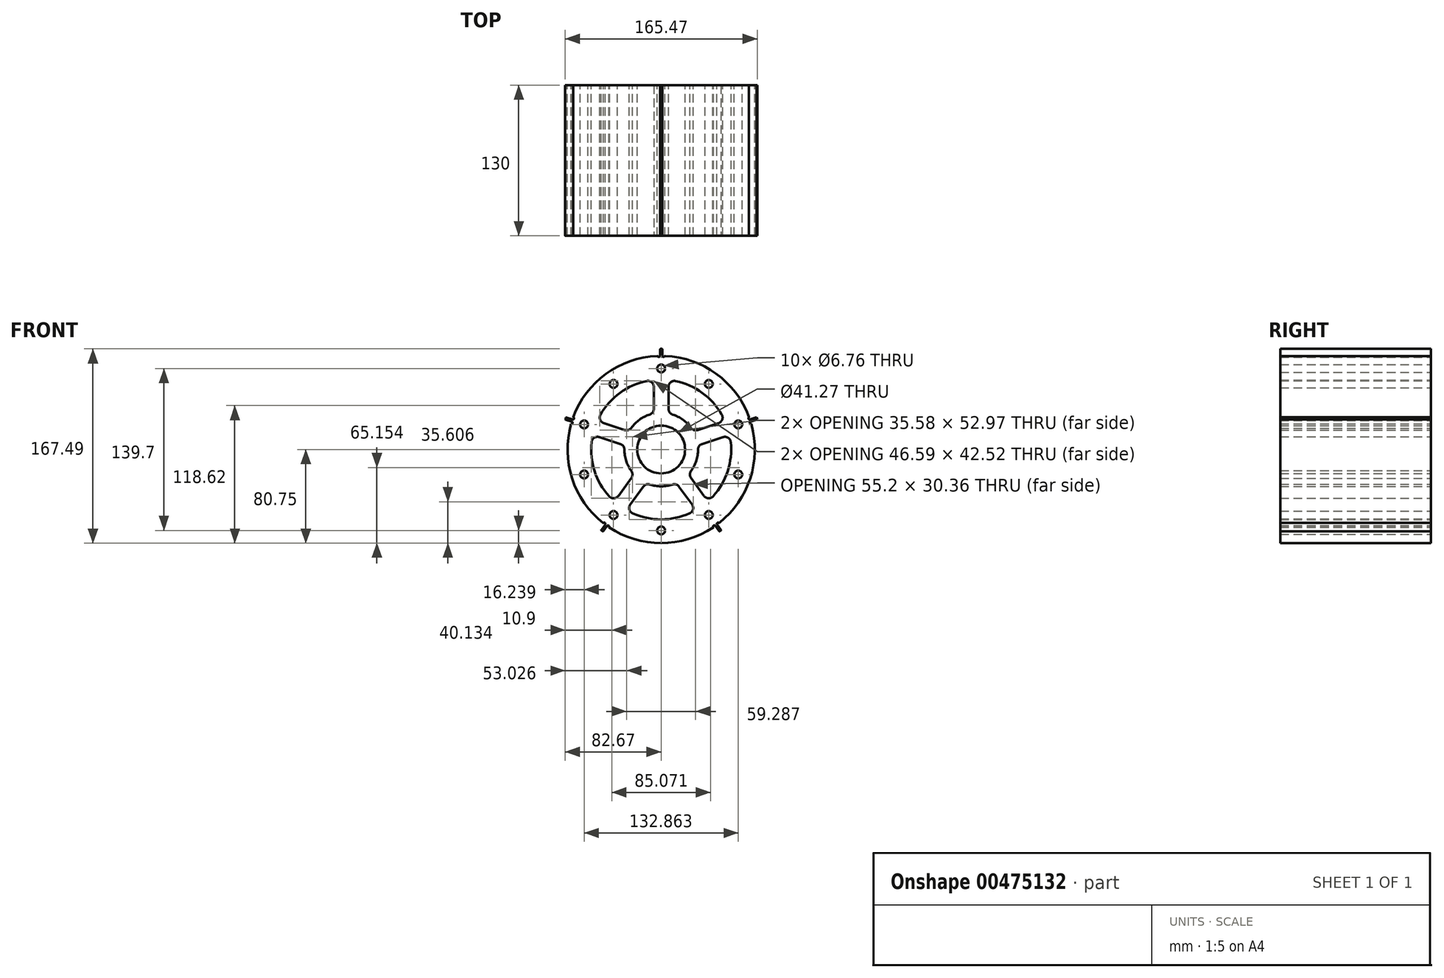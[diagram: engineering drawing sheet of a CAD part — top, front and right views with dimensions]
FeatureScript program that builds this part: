
annotation { "Feature Type Name" : "Feature", "Feature Type Description" : "" }
export const myFeature = defineFeature(function(context is Context, id is Id, definition is map)
    precondition{}
    {
        {
            var Q0;
            Q0=qCreatedBy(makeId("Front.planeOp"),FACE);
            var sketch = newSketch(context, id + "F0", { "sketchPlane" : qUnion([Q0])});
            skArc(sketch, "E0", {"start": v(-1, 80.74) * mm, "mid": v(-47.46, 65.33) * mm, "end": v(-76.48, 25.9) * mm});
            skLineSegment(sketch, "E1", {"start": v(0, 0) * mm, "end": v(0, 93.04) * mm, "construction": true});
            skLineSegment(sketch, "E2", {"start": v(-1, 86.74) * mm, "end": v(-1, 80.74) * mm});
            skLineSegment(sketch, "E3.MirrorCS", {"start": v(1, 86.74) * mm, "end": v(1, 80.74) * mm});
            skLineSegment(sketch, "E4", {"start": v(-1, 86.74) * mm, "end": v(1, 86.74) * mm});
            skLineSegment(sketch, "E5.1.0", {"start": v(-82.18, 27.75) * mm, "end": v(-76.48, 25.9) * mm});
            skLineSegment(sketch, "E5.1.1", {"start": v(-82.8, 25.85) * mm, "end": v(-82.18, 27.75) * mm});
            skLineSegment(sketch, "E5.1.2", {"start": v(-82.8, 25.85) * mm, "end": v(-77.1, 24) * mm});
            skLineSegment(sketch, "E5.2.0", {"start": v(-51.8, -69.58) * mm, "end": v(-48.27, -64.73) * mm});
            skLineSegment(sketch, "E5.2.1", {"start": v(-50.17, -70.76) * mm, "end": v(-51.8, -69.58) * mm});
            skLineSegment(sketch, "E5.2.2", {"start": v(-50.17, -70.76) * mm, "end": v(-46.65, -65.91) * mm});
            skLineSegment(sketch, "E5.3.0", {"start": v(50.17, -70.76) * mm, "end": v(46.65, -65.91) * mm});
            skLineSegment(sketch, "E5.3.1", {"start": v(51.8, -69.58) * mm, "end": v(50.17, -70.76) * mm});
            skLineSegment(sketch, "E5.3.2", {"start": v(51.8, -69.58) * mm, "end": v(48.27, -64.73) * mm});
            skArc(sketch, "E6.trimOffspring", {"start": v(-77.1, 24) * mm, "mid": v(-76.8, -24.95) * mm, "end": v(-48.27, -64.73) * mm});
            skArc(sketch, "E7.trimOffspring", {"start": v(76.48, 25.9) * mm, "mid": v(47.46, 65.33) * mm, "end": v(1, 80.74) * mm});
            skArc(sketch, "E8.trimOffspring", {"start": v(-46.65, -65.91) * mm, "mid": v(47.46, -65.33) * mm, "end": v(77.1, 24) * mm});
            skLineSegment(sketch, "E9.2.4.0", {"start": v(82.8, 25.85) * mm, "end": v(77.1, 24) * mm});
            skLineSegment(sketch, "E9.3.4.0", {"start": v(82.18, 27.75) * mm, "end": v(82.8, 25.85) * mm});
            skLineSegment(sketch, "E9.6.4.0", {"start": v(82.18, 27.75) * mm, "end": v(76.48, 25.9) * mm});
            skSolve(sketch);
        }
        {
            var Q0;
            Q0 = qSketchRegion(id + "F0", true);
            extrude(context, id + "F1", {"entities" : qUnion([Q0]), "depth" : 130 * mm});
        }
        {
            var Q0;
            Q0=qCreatedBy(makeId("Front.planeOp"),FACE);
            var sketch = newSketch(context, id + "F2", { "sketchPlane" : qUnion([Q0])});
            skCircle(sketch, "E10", {"center": v(0, 0) * mm, "radius": 20.64 * mm});
            skSolve(sketch);
        }
        {
            var Q0;
            Q0=makeQuery(id+"F2.imprint","IMPRINT",FACE,{"disambiguationData":[TD([[makeQuery(id+"F2.imprint","IMPRINT",EDGE,{"derivedFrom":sQuery(id+"F2.wireOp",EDGE,"E10")}),1.0]])]});
            var Q1;
            Q1=makeQuery(id+"F1.opExtrude","CAP_FACE",FACE,{"disambiguationData":[OSD([sQuery(id+"F0.wireOp",EDGE,"E0"),sQuery(id+"F0.wireOp",EDGE,"E2"),sQuery(id+"F0.wireOp",EDGE,"E3.MirrorCS"),sQuery(id+"F0.wireOp",EDGE,"E4"),sQuery(id+"F0.wireOp",EDGE,"E5.1.0"),sQuery(id+"F0.wireOp",EDGE,"E5.1.1"),sQuery(id+"F0.wireOp",EDGE,"E5.1.2"),sQuery(id+"F0.wireOp",EDGE,"E5.2.0"),sQuery(id+"F0.wireOp",EDGE,"E5.2.1"),sQuery(id+"F0.wireOp",EDGE,"E5.2.2"),sQuery(id+"F0.wireOp",EDGE,"E5.3.0"),sQuery(id+"F0.wireOp",EDGE,"E5.3.1"),sQuery(id+"F0.wireOp",EDGE,"E5.3.2"),sQuery(id+"F0.wireOp",EDGE,"E6.trimOffspring"),sQuery(id+"F0.wireOp",EDGE,"E7.trimOffspring"),sQuery(id+"F0.wireOp",EDGE,"E8.trimOffspring")])],"isStart":false});
            extrude(context, id + "F3", {"entities" : qUnion([Q0]), "operationType" : NewBodyOperationType.REMOVE, "endBound" : BoundingType.UP_TO_SURFACE, "endBoundEntityFace" : qUnion([Q1]), "depth" : 25.4 * mm});
        }
        {
            var Q0;
            Q0=qCreatedBy(makeId("Front.planeOp"),FACE);
            var sketch = newSketch(context, id + "F4", { "sketchPlane" : qUnion([Q0])});
            skLineSegment(sketch, "E11", {"start": v(9.9, 57.53) * mm, "end": v(9.9, 35.38) * mm});
            skLineSegment(sketch, "E12", {"start": v(35.38, 9.9) * mm, "end": v(57.53, 9.9) * mm});
            skArc(sketch, "E13", {"start": v(66.9, 23.04) * mm, "mid": v(50.03, 50.03) * mm, "end": v(23.04, 66.9) * mm});
            skArc(sketch, "E14", {"start": v(26.73, 14.97) * mm, "mid": v(21.67, 21.67) * mm, "end": v(14.97, 26.73) * mm});
            skArc(sketch, "E15.filletArc", {"start": v(26.73, 14.97) * mm, "mid": v(30.37, 11.27) * mm, "end": v(35.38, 9.9) * mm});
            skArc(sketch, "E16.filletArc", {"start": v(9.9, 35.38) * mm, "mid": v(11.27, 30.37) * mm, "end": v(14.97, 26.73) * mm});
            skArc(sketch, "E17.filletArc", {"start": v(23.04, 66.9) * mm, "mid": v(14.06, 65.6) * mm, "end": v(9.9, 57.53) * mm});
            skArc(sketch, "E18.filletArc", {"start": v(57.53, 9.9) * mm, "mid": v(65.6, 14.06) * mm, "end": v(66.9, 23.04) * mm});
            skLineSegment(sketch, "E19", {"start": v(0, 0) * mm, "end": v(0, 68.56) * mm, "construction": true});
            skLineSegment(sketch, "E20", {"start": v(0, 0) * mm, "end": v(60.99, 0) * mm, "construction": true});
            skLineSegment(sketch, "E21.1.0", {"start": v(-57.53, 9.9) * mm, "end": v(-35.38, 9.9) * mm});
            skArc(sketch, "E21.1.1", {"start": v(-66.9, 23.04) * mm, "mid": v(-65.6, 14.06) * mm, "end": v(-57.53, 9.9) * mm});
            skArc(sketch, "E21.1.2", {"start": v(-23.04, 66.9) * mm, "mid": v(-50.03, 50.03) * mm, "end": v(-66.9, 23.04) * mm});
            skArc(sketch, "E21.1.3", {"start": v(-9.9, 57.53) * mm, "mid": v(-14.06, 65.6) * mm, "end": v(-23.04, 66.9) * mm});
            skLineSegment(sketch, "E21.1.4", {"start": v(-9.9, 35.38) * mm, "end": v(-9.9, 57.53) * mm});
            skArc(sketch, "E21.1.5", {"start": v(-14.97, 26.73) * mm, "mid": v(-11.27, 30.37) * mm, "end": v(-9.9, 35.38) * mm});
            skArc(sketch, "E21.1.6", {"start": v(-35.38, 9.9) * mm, "mid": v(-30.37, 11.27) * mm, "end": v(-26.73, 14.97) * mm});
            skArc(sketch, "E21.1.7", {"start": v(-14.97, 26.73) * mm, "mid": v(-21.67, 21.67) * mm, "end": v(-26.73, 14.97) * mm});
            skLineSegment(sketch, "E21.2.0", {"start": v(-9.9, -57.53) * mm, "end": v(-9.9, -35.38) * mm});
            skArc(sketch, "E21.2.1", {"start": v(-23.04, -66.9) * mm, "mid": v(-14.06, -65.6) * mm, "end": v(-9.9, -57.53) * mm});
            skArc(sketch, "E21.2.2", {"start": v(-66.9, -23.04) * mm, "mid": v(-50.03, -50.03) * mm, "end": v(-23.04, -66.9) * mm});
            skArc(sketch, "E21.2.3", {"start": v(-57.53, -9.9) * mm, "mid": v(-65.6, -14.06) * mm, "end": v(-66.9, -23.04) * mm});
            skLineSegment(sketch, "E21.2.4", {"start": v(-35.38, -9.9) * mm, "end": v(-57.53, -9.9) * mm});
            skArc(sketch, "E21.2.5", {"start": v(-26.73, -14.97) * mm, "mid": v(-30.37, -11.27) * mm, "end": v(-35.38, -9.9) * mm});
            skArc(sketch, "E21.2.6", {"start": v(-9.9, -35.38) * mm, "mid": v(-11.27, -30.37) * mm, "end": v(-14.97, -26.73) * mm});
            skArc(sketch, "E21.2.7", {"start": v(-26.73, -14.97) * mm, "mid": v(-21.67, -21.67) * mm, "end": v(-14.97, -26.73) * mm});
            skLineSegment(sketch, "E21.3.0", {"start": v(57.53, -9.9) * mm, "end": v(35.38, -9.9) * mm});
            skArc(sketch, "E21.3.1", {"start": v(66.9, -23.04) * mm, "mid": v(65.6, -14.06) * mm, "end": v(57.53, -9.9) * mm});
            skArc(sketch, "E21.3.2", {"start": v(23.04, -66.9) * mm, "mid": v(50.03, -50.03) * mm, "end": v(66.9, -23.04) * mm});
            skArc(sketch, "E21.3.3", {"start": v(9.9, -57.53) * mm, "mid": v(14.06, -65.6) * mm, "end": v(23.04, -66.9) * mm});
            skLineSegment(sketch, "E21.3.4", {"start": v(9.9, -35.38) * mm, "end": v(9.9, -57.53) * mm});
            skArc(sketch, "E21.3.5", {"start": v(14.97, -26.73) * mm, "mid": v(11.27, -30.37) * mm, "end": v(9.9, -35.38) * mm});
            skArc(sketch, "E21.3.6", {"start": v(35.38, -9.9) * mm, "mid": v(30.37, -11.27) * mm, "end": v(26.73, -14.97) * mm});
            skArc(sketch, "E21.3.7", {"start": v(14.97, -26.73) * mm, "mid": v(21.67, -21.67) * mm, "end": v(26.73, -14.97) * mm});
            skSolve(sketch);
        }
        {
            var Q0;
            Q0=makeQuery(id+"F1.opExtrude","CAP_FACE",FACE,{"disambiguationData":[OSD([sQuery(id+"F0.wireOp",EDGE,"E0"),sQuery(id+"F0.wireOp",EDGE,"E2"),sQuery(id+"F0.wireOp",EDGE,"E3.MirrorCS"),sQuery(id+"F0.wireOp",EDGE,"E4"),sQuery(id+"F0.wireOp",EDGE,"E5.1.0"),sQuery(id+"F0.wireOp",EDGE,"E5.1.1"),sQuery(id+"F0.wireOp",EDGE,"E5.1.2"),sQuery(id+"F0.wireOp",EDGE,"E5.2.0"),sQuery(id+"F0.wireOp",EDGE,"E5.2.1"),sQuery(id+"F0.wireOp",EDGE,"E5.2.2"),sQuery(id+"F0.wireOp",EDGE,"E5.3.0"),sQuery(id+"F0.wireOp",EDGE,"E5.3.1"),sQuery(id+"F0.wireOp",EDGE,"E5.3.2"),sQuery(id+"F0.wireOp",EDGE,"E6.trimOffspring"),sQuery(id+"F0.wireOp",EDGE,"E7.trimOffspring"),sQuery(id+"F0.wireOp",EDGE,"E8.trimOffspring")])],"isStart":true});
            var sketch = newSketch(context, id + "F5", { "sketchPlane" : qUnion([Q0])});
            skLineSegment(sketch, "E22", {"start": v(-1, 80.74) * mm, "end": v(-7.67, 80.74) * mm, "construction": true});
            skCircle(sketch, "E23", {"center": v(-2.02, 80.74) * mm, "radius": 1.02 * mm});
            skCircle(sketch, "E24.MirrorC", {"center": v(2.02, 80.74) * mm, "radius": 1.02 * mm});
            skCircle(sketch, "E25.1.0", {"center": v(-76.17, 26.87) * mm, "radius": 1.02 * mm});
            skCircle(sketch, "E25.1.1", {"center": v(-77.41, 23.03) * mm, "radius": 1.02 * mm});
            skCircle(sketch, "E25.2.0", {"center": v(-49.1, -64.14) * mm, "radius": 1.02 * mm});
            skCircle(sketch, "E25.2.1", {"center": v(-45.83, -66.5) * mm, "radius": 1.02 * mm});
            skCircle(sketch, "E25.3.0", {"center": v(45.83, -66.5) * mm, "radius": 1.02 * mm});
            skCircle(sketch, "E25.3.1", {"center": v(49.1, -64.14) * mm, "radius": 1.02 * mm});
            skPoint(sketch, "E25.center", {"position": v(0, 0) * mm});
            skCircle(sketch, "E26.1.4.0", {"center": v(77.41, 23.03) * mm, "radius": 1.02 * mm});
            skCircle(sketch, "E26.2.4.0", {"center": v(76.17, 26.87) * mm, "radius": 1.02 * mm});
            skSolve(sketch);
        }
        {
            var Q0;
            Q0 = qSketchRegion(id + "F5", true);
            extrude(context, id + "F6", {"entities" : qUnion([Q0]), "operationType" : NewBodyOperationType.REMOVE, "endBound" : BoundingType.THROUGH_ALL, "oppositeDirection" : true, "depth" : 25.4 * mm});
        }
        {
            var Q0;
            Q0=makeQuery(id+"F1.opExtrude","SWEPT_EDGE",EDGE,{"disambiguationData":[OSD([sQuery(id+"F0.wireOp",EDGE,"E2"),sQuery(id+"F0.wireOp",EDGE,"E4")])]});
            var Q1;
            Q1=makeQuery(id+"F1.opExtrude","SWEPT_EDGE",EDGE,{"disambiguationData":[OSD([sQuery(id+"F0.wireOp",EDGE,"E3.MirrorCS"),sQuery(id+"F0.wireOp",EDGE,"E4")])]});
            var Q2;
            Q2=makeQuery(id+"F6.boolean.opBoolean","INTERSECT",EDGE,{"derivedFrom":[makeQuery(id+"F1.opExtrude","SWEPT_FACE",FACE,{"disambiguationData":[OSD([sQuery(id+"F0.wireOp",EDGE,"E0")])]}),makeQuery(id+"F6.opExtrude","SWEPT_FACE",FACE,{"disambiguationData":[OSD([sQuery(id+"F5.wireOp",EDGE,"E24.MirrorC")])]})]});
            var Q3;
            Q3=makeQuery(id+"F6.boolean.opBoolean","INTERSECT",EDGE,{"derivedFrom":[makeQuery(id+"F1.opExtrude","SWEPT_FACE",FACE,{"disambiguationData":[OSD([sQuery(id+"F0.wireOp",EDGE,"E7.trimOffspring")])]}),makeQuery(id+"F6.opExtrude","SWEPT_FACE",FACE,{"disambiguationData":[OSD([sQuery(id+"F5.wireOp",EDGE,"E23")])]})]});
            var Q4;
            Q4=makeQuery(id+"F6.boolean.opBoolean","INTERSECT",EDGE,{"derivedFrom":[makeQuery(id+"F1.opExtrude","SWEPT_FACE",FACE,{"disambiguationData":[OSD([sQuery(id+"F0.wireOp",EDGE,"E0")])]}),makeQuery(id+"F6.opExtrude","SWEPT_FACE",FACE,{"disambiguationData":[OSD([sQuery(id+"F5.wireOp",EDGE,"E25.3.1")])]})]});
            var Q5;
            Q5=makeQuery(id+"F1.opExtrude","SWEPT_EDGE",EDGE,{"disambiguationData":[OSD([sQuery(id+"F0.wireOp",EDGE,"E5.1.0"),sQuery(id+"F0.wireOp",EDGE,"E5.1.1")])]});
            var Q6;
            Q6=makeQuery(id+"F1.opExtrude","SWEPT_EDGE",EDGE,{"disambiguationData":[OSD([sQuery(id+"F0.wireOp",EDGE,"E5.1.1"),sQuery(id+"F0.wireOp",EDGE,"E5.1.2")])]});
            var Q7;
            Q7=makeQuery(id+"F6.boolean.opBoolean","INTERSECT",EDGE,{"derivedFrom":[makeQuery(id+"F1.opExtrude","SWEPT_FACE",FACE,{"disambiguationData":[OSD([sQuery(id+"F0.wireOp",EDGE,"E6.trimOffspring")])]}),makeQuery(id+"F6.opExtrude","SWEPT_FACE",FACE,{"disambiguationData":[OSD([sQuery(id+"F5.wireOp",EDGE,"E25.3.0")])]})]});
            var Q8;
            Q8=makeQuery(id+"F6.boolean.opBoolean","INTERSECT",EDGE,{"derivedFrom":[makeQuery(id+"F1.opExtrude","SWEPT_FACE",FACE,{"disambiguationData":[OSD([sQuery(id+"F0.wireOp",EDGE,"E6.trimOffspring")])]}),makeQuery(id+"F6.opExtrude","SWEPT_FACE",FACE,{"disambiguationData":[OSD([sQuery(id+"F5.wireOp",EDGE,"E25.2.1")])]})]});
            var Q9;
            Q9=makeQuery(id+"F1.opExtrude","SWEPT_EDGE",EDGE,{"disambiguationData":[OSD([sQuery(id+"F0.wireOp",EDGE,"E5.2.0"),sQuery(id+"F0.wireOp",EDGE,"E5.2.1")])]});
            var Q10;
            Q10=makeQuery(id+"F1.opExtrude","SWEPT_EDGE",EDGE,{"disambiguationData":[OSD([sQuery(id+"F0.wireOp",EDGE,"E5.2.1"),sQuery(id+"F0.wireOp",EDGE,"E5.2.2")])]});
            var Q11;
            Q11=makeQuery(id+"F6.boolean.opBoolean","INTERSECT",EDGE,{"derivedFrom":[makeQuery(id+"F1.opExtrude","SWEPT_FACE",FACE,{"disambiguationData":[OSD([sQuery(id+"F0.wireOp",EDGE,"E8.trimOffspring")])]}),makeQuery(id+"F6.opExtrude","SWEPT_FACE",FACE,{"disambiguationData":[OSD([sQuery(id+"F5.wireOp",EDGE,"E25.2.0")])]})]});
            var Q12;
            Q12=makeQuery(id+"F6.boolean.opBoolean","INTERSECT",EDGE,{"derivedFrom":[makeQuery(id+"F1.opExtrude","SWEPT_FACE",FACE,{"disambiguationData":[OSD([sQuery(id+"F0.wireOp",EDGE,"E8.trimOffspring")])]}),makeQuery(id+"F6.opExtrude","SWEPT_FACE",FACE,{"disambiguationData":[OSD([sQuery(id+"F5.wireOp",EDGE,"E25.1.1")])]})]});
            var Q13;
            Q13=makeQuery(id+"F1.opExtrude","SWEPT_EDGE",EDGE,{"disambiguationData":[OSD([sQuery(id+"F0.wireOp",EDGE,"E5.3.0"),sQuery(id+"F0.wireOp",EDGE,"E5.3.1")])]});
            var Q14;
            Q14=makeQuery(id+"F1.opExtrude","SWEPT_EDGE",EDGE,{"disambiguationData":[OSD([sQuery(id+"F0.wireOp",EDGE,"E5.3.1"),sQuery(id+"F0.wireOp",EDGE,"E5.3.2")])]});
            var Q15;
            Q15=makeQuery(id+"F6.boolean.opBoolean","INTERSECT",EDGE,{"derivedFrom":[makeQuery(id+"F1.opExtrude","SWEPT_FACE",FACE,{"disambiguationData":[OSD([sQuery(id+"F0.wireOp",EDGE,"E7.trimOffspring")])]}),makeQuery(id+"F6.opExtrude","SWEPT_FACE",FACE,{"disambiguationData":[OSD([sQuery(id+"F5.wireOp",EDGE,"E25.1.0")])]})]});
            fillet(context, id + "F7", {"entities" : qUnion([Q0, Q1, Q2, Q3, Q4, Q5, Q6, Q7, Q8, Q9, Q10, Q11, Q12, Q13, Q14, Q15]), "radius" : 0.5 * mm, "tangentPropagation" : true, "allowEdgeOverflow" : false});
        }
        {
            var Q0;
            Q0=makeQuery(id+"F1.opExtrude","CAP_FACE",FACE,{"disambiguationData":[OSD([sQuery(id+"F0.wireOp",EDGE,"E0"),sQuery(id+"F0.wireOp",EDGE,"E2"),sQuery(id+"F0.wireOp",EDGE,"E3.MirrorCS"),sQuery(id+"F0.wireOp",EDGE,"E4"),sQuery(id+"F0.wireOp",EDGE,"E5.1.0"),sQuery(id+"F0.wireOp",EDGE,"E5.1.1"),sQuery(id+"F0.wireOp",EDGE,"E5.1.2"),sQuery(id+"F0.wireOp",EDGE,"E5.2.0"),sQuery(id+"F0.wireOp",EDGE,"E5.2.1"),sQuery(id+"F0.wireOp",EDGE,"E5.2.2"),sQuery(id+"F0.wireOp",EDGE,"E5.3.0"),sQuery(id+"F0.wireOp",EDGE,"E5.3.1"),sQuery(id+"F0.wireOp",EDGE,"E5.3.2"),sQuery(id+"F0.wireOp",EDGE,"E6.trimOffspring"),sQuery(id+"F0.wireOp",EDGE,"E7.trimOffspring"),sQuery(id+"F0.wireOp",EDGE,"E8.trimOffspring"),sQuery(id+"F0.wireOp",EDGE,"E9.2.4.0"),sQuery(id+"F0.wireOp",EDGE,"E9.3.4.0"),sQuery(id+"F0.wireOp",EDGE,"E9.6.4.0")])],"isStart":true});
            var sketch = newSketch(context, id + "F8", { "sketchPlane" : qUnion([Q0])});
            skArc(sketch, "E27", {"start": v(-6.35, 59.99) * mm, "mid": v(-35.46, 48.8) * mm, "end": v(-55.1, 24.58) * mm});
            skArc(sketch, "E28", {"start": v(-6.35, 31.1) * mm, "mid": v(-18.66, 25.69) * mm, "end": v(-27.62, 15.65) * mm});
            skLineSegment(sketch, "E29", {"start": v(-6.35, 59.99) * mm, "end": v(-6.35, 31.1) * mm});
            skLineSegment(sketch, "E30", {"start": v(6.35, 59.99) * mm, "end": v(6.35, 31.1) * mm});
            skLineSegment(sketch, "E31.1.0", {"start": v(-59.02, 12.5) * mm, "end": v(-31.55, 3.57) * mm});
            skLineSegment(sketch, "E31.1.1", {"start": v(-55.1, 24.58) * mm, "end": v(-27.62, 15.65) * mm});
            skLineSegment(sketch, "E31.2.0", {"start": v(-30.12, -52.27) * mm, "end": v(-13.15, -28.9) * mm});
            skLineSegment(sketch, "E31.2.1", {"start": v(-40.4, -44.8) * mm, "end": v(-23.42, -21.43) * mm});
            skLineSegment(sketch, "E31.3.0", {"start": v(40.4, -44.8) * mm, "end": v(23.42, -21.43) * mm});
            skLineSegment(sketch, "E31.3.1", {"start": v(30.12, -52.27) * mm, "end": v(13.15, -28.9) * mm});
            skLineSegment(sketch, "E31.4.0", {"start": v(55.1, 24.58) * mm, "end": v(27.62, 15.65) * mm});
            skLineSegment(sketch, "E31.4.1", {"start": v(59.02, 12.5) * mm, "end": v(31.55, 3.57) * mm});
            skArc(sketch, "E32.trimOffspring", {"start": v(-59.02, 12.5) * mm, "mid": v(-57.37, -18.64) * mm, "end": v(-40.4, -44.8) * mm});
            skArc(sketch, "E33.trimOffspring", {"start": v(-31.55, 3.57) * mm, "mid": v(-30.2, -9.81) * mm, "end": v(-23.42, -21.43) * mm});
            skArc(sketch, "E34.trimOffspring", {"start": v(-13.15, -28.9) * mm, "mid": v(0, -31.75) * mm, "end": v(13.15, -28.9) * mm});
            skArc(sketch, "E35.trimOffspring", {"start": v(-30.12, -52.27) * mm, "mid": v(0, -60.33) * mm, "end": v(30.12, -52.27) * mm});
            skArc(sketch, "E36.trimOffspring", {"start": v(40.4, -44.8) * mm, "mid": v(57.37, -18.64) * mm, "end": v(59.02, 12.5) * mm});
            skArc(sketch, "E37.trimOffspring", {"start": v(23.42, -21.43) * mm, "mid": v(30.2, -9.81) * mm, "end": v(31.55, 3.57) * mm});
            skArc(sketch, "E38.trimOffspring", {"start": v(27.62, 15.65) * mm, "mid": v(18.66, 25.69) * mm, "end": v(6.35, 31.1) * mm});
            skArc(sketch, "E39.trimOffspring", {"start": v(55.1, 24.58) * mm, "mid": v(35.46, 48.8) * mm, "end": v(6.35, 59.99) * mm});
            skSolve(sketch);
        }
        {
            var Q0;
            Q0=makeQuery(id+"F8.imprint","IMPRINT",FACE,{"disambiguationData":[TD([[makeQuery(id+"F8.imprint","IMPRINT",EDGE,{"derivedFrom":sQuery(id+"F8.wireOp",EDGE,"E27")}),1.0]])]});
            var Q1;
            Q1=makeQuery(id+"F8.imprint","IMPRINT",FACE,{"disambiguationData":[TD([[makeQuery(id+"F8.imprint","IMPRINT",EDGE,{"derivedFrom":sQuery(id+"F8.wireOp",EDGE,"E30")}),1.0]])]});
            var Q2;
            Q2=makeQuery(id+"F8.imprint","IMPRINT",FACE,{"disambiguationData":[TD([[makeQuery(id+"F8.imprint","IMPRINT",EDGE,{"derivedFrom":sQuery(id+"F8.wireOp",EDGE,"E31.3.0")}),-1.0]])]});
            var Q3;
            Q3=makeQuery(id+"F8.imprint","IMPRINT",FACE,{"disambiguationData":[TD([[makeQuery(id+"F8.imprint","IMPRINT",EDGE,{"derivedFrom":sQuery(id+"F8.wireOp",EDGE,"E31.2.0")}),-1.0]])]});
            var Q4;
            Q4=makeQuery(id+"F8.imprint","IMPRINT",FACE,{"disambiguationData":[TD([[makeQuery(id+"F8.imprint","IMPRINT",EDGE,{"derivedFrom":sQuery(id+"F8.wireOp",EDGE,"E31.1.0")}),-1.0]])]});
            extrude(context, id + "F9", {"entities" : qUnion([Q0, Q1, Q2, Q3, Q4]), "operationType" : NewBodyOperationType.REMOVE, "endBound" : BoundingType.THROUGH_ALL, "oppositeDirection" : true, "depth" : 25.4 * mm});
        }
        {
            var Q0;
            Q0=makeQuery(id+"F9.boolean.opBoolean","COPY",EDGE,{"derivedFrom":makeQuery(id+"F9.opExtrude","SWEPT_EDGE",EDGE,{"disambiguationData":[OSD([sQuery(id+"F8.wireOp",EDGE,"E27"),sQuery(id+"F8.wireOp",EDGE,"E31.1.1")])]})});
            var Q1;
            Q1=makeQuery(id+"F9.boolean.opBoolean","COPY",EDGE,{"derivedFrom":makeQuery(id+"F9.opExtrude","SWEPT_EDGE",EDGE,{"disambiguationData":[OSD([sQuery(id+"F8.wireOp",EDGE,"E28"),sQuery(id+"F8.wireOp",EDGE,"E31.1.1")])]})});
            var Q2;
            Q2=makeQuery(id+"F9.boolean.opBoolean","COPY",EDGE,{"derivedFrom":makeQuery(id+"F9.opExtrude","SWEPT_EDGE",EDGE,{"disambiguationData":[OSD([sQuery(id+"F8.wireOp",EDGE,"E28"),sQuery(id+"F8.wireOp",EDGE,"E29")])]})});
            var Q3;
            Q3=makeQuery(id+"F9.boolean.opBoolean","COPY",EDGE,{"derivedFrom":makeQuery(id+"F9.opExtrude","SWEPT_EDGE",EDGE,{"disambiguationData":[OSD([sQuery(id+"F8.wireOp",EDGE,"E27"),sQuery(id+"F8.wireOp",EDGE,"E29")])]})});
            var Q4;
            Q4=makeQuery(id+"F9.boolean.opBoolean","COPY",EDGE,{"derivedFrom":makeQuery(id+"F9.opExtrude","SWEPT_EDGE",EDGE,{"disambiguationData":[OSD([sQuery(id+"F8.wireOp",EDGE,"E31.4.0"),sQuery(id+"F8.wireOp",EDGE,"E39.trimOffspring")])]})});
            var Q5;
            Q5=makeQuery(id+"F9.boolean.opBoolean","COPY",EDGE,{"derivedFrom":makeQuery(id+"F9.opExtrude","SWEPT_EDGE",EDGE,{"disambiguationData":[OSD([sQuery(id+"F8.wireOp",EDGE,"E31.4.0"),sQuery(id+"F8.wireOp",EDGE,"E38.trimOffspring")])]})});
            var Q6;
            Q6=makeQuery(id+"F9.boolean.opBoolean","COPY",EDGE,{"derivedFrom":makeQuery(id+"F9.opExtrude","SWEPT_EDGE",EDGE,{"disambiguationData":[OSD([sQuery(id+"F8.wireOp",EDGE,"E30"),sQuery(id+"F8.wireOp",EDGE,"E38.trimOffspring")])]})});
            var Q7;
            Q7=makeQuery(id+"F9.boolean.opBoolean","COPY",EDGE,{"derivedFrom":makeQuery(id+"F9.opExtrude","SWEPT_EDGE",EDGE,{"disambiguationData":[OSD([sQuery(id+"F8.wireOp",EDGE,"E30"),sQuery(id+"F8.wireOp",EDGE,"E39.trimOffspring")])]})});
            var Q8;
            Q8=makeQuery(id+"F9.boolean.opBoolean","COPY",EDGE,{"derivedFrom":makeQuery(id+"F9.opExtrude","SWEPT_EDGE",EDGE,{"disambiguationData":[OSD([sQuery(id+"F8.wireOp",EDGE,"E31.4.1"),sQuery(id+"F8.wireOp",EDGE,"E36.trimOffspring")])]})});
            var Q9;
            Q9=makeQuery(id+"F9.boolean.opBoolean","COPY",EDGE,{"derivedFrom":makeQuery(id+"F9.opExtrude","SWEPT_EDGE",EDGE,{"disambiguationData":[OSD([sQuery(id+"F8.wireOp",EDGE,"E31.3.0"),sQuery(id+"F8.wireOp",EDGE,"E36.trimOffspring")])]})});
            var Q10;
            Q10=makeQuery(id+"F9.boolean.opBoolean","COPY",EDGE,{"derivedFrom":makeQuery(id+"F9.opExtrude","SWEPT_EDGE",EDGE,{"disambiguationData":[OSD([sQuery(id+"F8.wireOp",EDGE,"E31.3.0"),sQuery(id+"F8.wireOp",EDGE,"E37.trimOffspring")])]})});
            var Q11;
            Q11=makeQuery(id+"F9.boolean.opBoolean","COPY",EDGE,{"derivedFrom":makeQuery(id+"F9.opExtrude","SWEPT_EDGE",EDGE,{"disambiguationData":[OSD([sQuery(id+"F8.wireOp",EDGE,"E31.4.1"),sQuery(id+"F8.wireOp",EDGE,"E37.trimOffspring")])]})});
            var Q12;
            Q12=makeQuery(id+"F9.boolean.opBoolean","COPY",EDGE,{"derivedFrom":makeQuery(id+"F9.opExtrude","SWEPT_EDGE",EDGE,{"disambiguationData":[OSD([sQuery(id+"F8.wireOp",EDGE,"E31.2.0"),sQuery(id+"F8.wireOp",EDGE,"E35.trimOffspring")])]})});
            var Q13;
            Q13=makeQuery(id+"F9.boolean.opBoolean","COPY",EDGE,{"derivedFrom":makeQuery(id+"F9.opExtrude","SWEPT_EDGE",EDGE,{"disambiguationData":[OSD([sQuery(id+"F8.wireOp",EDGE,"E31.3.1"),sQuery(id+"F8.wireOp",EDGE,"E35.trimOffspring")])]})});
            var Q14;
            Q14=makeQuery(id+"F9.boolean.opBoolean","COPY",EDGE,{"derivedFrom":makeQuery(id+"F9.opExtrude","SWEPT_EDGE",EDGE,{"disambiguationData":[OSD([sQuery(id+"F8.wireOp",EDGE,"E31.3.1"),sQuery(id+"F8.wireOp",EDGE,"E34.trimOffspring")])]})});
            var Q15;
            Q15=makeQuery(id+"F9.boolean.opBoolean","COPY",EDGE,{"derivedFrom":makeQuery(id+"F9.opExtrude","SWEPT_EDGE",EDGE,{"disambiguationData":[OSD([sQuery(id+"F8.wireOp",EDGE,"E31.2.0"),sQuery(id+"F8.wireOp",EDGE,"E34.trimOffspring")])]})});
            var Q16;
            Q16=makeQuery(id+"F9.boolean.opBoolean","COPY",EDGE,{"derivedFrom":makeQuery(id+"F9.opExtrude","SWEPT_EDGE",EDGE,{"disambiguationData":[OSD([sQuery(id+"F8.wireOp",EDGE,"E31.1.0"),sQuery(id+"F8.wireOp",EDGE,"E33.trimOffspring")])]})});
            var Q17;
            Q17=makeQuery(id+"F9.boolean.opBoolean","COPY",EDGE,{"derivedFrom":makeQuery(id+"F9.opExtrude","SWEPT_EDGE",EDGE,{"disambiguationData":[OSD([sQuery(id+"F8.wireOp",EDGE,"E31.2.1"),sQuery(id+"F8.wireOp",EDGE,"E33.trimOffspring")])]})});
            var Q18;
            Q18=makeQuery(id+"F9.boolean.opBoolean","COPY",EDGE,{"derivedFrom":makeQuery(id+"F9.opExtrude","SWEPT_EDGE",EDGE,{"disambiguationData":[OSD([sQuery(id+"F8.wireOp",EDGE,"E31.2.1"),sQuery(id+"F8.wireOp",EDGE,"E32.trimOffspring")])]})});
            var Q19;
            Q19=makeQuery(id+"F9.boolean.opBoolean","COPY",EDGE,{"derivedFrom":makeQuery(id+"F9.opExtrude","SWEPT_EDGE",EDGE,{"disambiguationData":[OSD([sQuery(id+"F8.wireOp",EDGE,"E31.1.0"),sQuery(id+"F8.wireOp",EDGE,"E32.trimOffspring")])]})});
            fillet(context, id + "F10", {"entities" : qUnion([Q0, Q1, Q2, Q3, Q4, Q5, Q6, Q7, Q8, Q9, Q10, Q11, Q12, Q13, Q14, Q15, Q16, Q17, Q18, Q19]), "radius" : 5.08 * mm, "tangentPropagation" : true, "allowEdgeOverflow" : false});
        }
        {
            var Q0;
            Q0=makeQuery(id+"F1.opExtrude","CAP_FACE",FACE,{"disambiguationData":[OSD([sQuery(id+"F0.wireOp",EDGE,"E0"),sQuery(id+"F0.wireOp",EDGE,"E2"),sQuery(id+"F0.wireOp",EDGE,"E3.MirrorCS"),sQuery(id+"F0.wireOp",EDGE,"E4"),sQuery(id+"F0.wireOp",EDGE,"E5.1.0"),sQuery(id+"F0.wireOp",EDGE,"E5.1.1"),sQuery(id+"F0.wireOp",EDGE,"E5.1.2"),sQuery(id+"F0.wireOp",EDGE,"E5.2.0"),sQuery(id+"F0.wireOp",EDGE,"E5.2.1"),sQuery(id+"F0.wireOp",EDGE,"E5.2.2"),sQuery(id+"F0.wireOp",EDGE,"E5.3.0"),sQuery(id+"F0.wireOp",EDGE,"E5.3.1"),sQuery(id+"F0.wireOp",EDGE,"E5.3.2"),sQuery(id+"F0.wireOp",EDGE,"E6.trimOffspring"),sQuery(id+"F0.wireOp",EDGE,"E7.trimOffspring"),sQuery(id+"F0.wireOp",EDGE,"E8.trimOffspring"),sQuery(id+"F0.wireOp",EDGE,"E9.2.4.0"),sQuery(id+"F0.wireOp",EDGE,"E9.3.4.0"),sQuery(id+"F0.wireOp",EDGE,"E9.6.4.0")])],"isStart":true});
            var sketch = newSketch(context, id + "F11", { "sketchPlane" : qUnion([Q0])});
            skCircle(sketch, "E40", {"center": v(0, 0) * mm, "radius": 69.85 * mm, "construction": true});
            skLineSegment(sketch, "E41", {"start": v(0, 85.6) * mm, "end": v(0, 68.09) * mm, "construction": true});
            skPoint(sketch, "E41.startSnap0", {"position": v(0, 86.74) * mm});
            skPoint(sketch, "E42", {"position": v(0, 69.85) * mm});
            skPoint(sketch, "E43.1.0", {"position": v(-41.06, 56.5) * mm});
            skPoint(sketch, "E43.2.0", {"position": v(-66.43, 21.58) * mm});
            skPoint(sketch, "E43.3.0", {"position": v(-66.43, -21.58) * mm});
            skPoint(sketch, "E43.4.0", {"position": v(-41.06, -56.5) * mm});
            skPoint(sketch, "E43.5.0", {"position": v(0, -69.85) * mm});
            skPoint(sketch, "E43.6.0", {"position": v(41.06, -56.5) * mm});
            skPoint(sketch, "E43.7.0", {"position": v(66.43, -21.58) * mm});
            skPoint(sketch, "E44.0.8.0", {"position": v(66.43, 21.58) * mm});
            skPoint(sketch, "E44.0.9.0", {"position": v(41.06, 56.5) * mm});
            skSolve(sketch);
        }
        {
            var Q0;
            Q0=sQuery(id+"F11.wireOp",VERTEX,"E42");
            var Q1;
            Q1=sQuery(id+"F11.wireOp",VERTEX,"E43.1.0");
            var Q2;
            Q2=sQuery(id+"F11.wireOp",VERTEX,"E43.2.0");
            var Q3;
            Q3=sQuery(id+"F11.wireOp",VERTEX,"E43.3.0");
            var Q4;
            Q4=sQuery(id+"F11.wireOp",VERTEX,"E43.4.0");
            var Q5;
            Q5=sQuery(id+"F11.wireOp",VERTEX,"E43.5.0");
            var Q6;
            Q6=sQuery(id+"F11.wireOp",VERTEX,"E43.6.0");
            var Q7;
            Q7=sQuery(id+"F11.wireOp",VERTEX,"E43.7.0");
            var Q8;
            Q8=sQuery(id+"F11.wireOp",VERTEX,"E44.0.8.0");
            var Q9;
            Q9=sQuery(id+"F11.wireOp",VERTEX,"E44.0.9.0");
            var Q10;
            Q10=makeQuery(id+"F1.opExtrude","SWEPT_BODY",BODY,{"disambiguationData":[OSD([sQuery(id+"F0.wireOp",EDGE,"E0"),sQuery(id+"F0.wireOp",EDGE,"E2"),sQuery(id+"F0.wireOp",EDGE,"E3.MirrorCS"),sQuery(id+"F0.wireOp",EDGE,"E4"),sQuery(id+"F0.wireOp",EDGE,"E5.1.0"),sQuery(id+"F0.wireOp",EDGE,"E5.1.1"),sQuery(id+"F0.wireOp",EDGE,"E5.1.2"),sQuery(id+"F0.wireOp",EDGE,"E5.2.0"),sQuery(id+"F0.wireOp",EDGE,"E5.2.1"),sQuery(id+"F0.wireOp",EDGE,"E5.2.2"),sQuery(id+"F0.wireOp",EDGE,"E5.3.0"),sQuery(id+"F0.wireOp",EDGE,"E5.3.1"),sQuery(id+"F0.wireOp",EDGE,"E5.3.2"),sQuery(id+"F0.wireOp",EDGE,"E6.trimOffspring"),sQuery(id+"F0.wireOp",EDGE,"E7.trimOffspring"),sQuery(id+"F0.wireOp",EDGE,"E8.trimOffspring"),sQuery(id+"F0.wireOp",EDGE,"E9.2.4.0"),sQuery(id+"F0.wireOp",EDGE,"E9.3.4.0"),sQuery(id+"F0.wireOp",EDGE,"E9.6.4.0")])]});
            hole(context, id + "F12", {"style" : HoleStyle.SIMPLE, "endStyle" : HoleEndStyle.THROUGH, "standardTappedOrClearance" : lookupTablePath({ "standard" : "ANSI", "fit" : "Normal (ASME)", "size" : "1/4", "type" : "Clearance" }), "standardBlindInLast" : lookupTablePath({ "fit" : "Free", "standard" : "ANSI", "size" : "1/4", "type" : "Clearance" }), "holeDiameter" : 6.76 * mm, "tappedDepth" : 25.4 * mm, "tapClearance" : 3, "startFromSketch" : true, "locations" : qUnion([Q0, Q1, Q2, Q3, Q4, Q5, Q6, Q7, Q8, Q9]), "scope" : qUnion([Q10])});
        }
    });
